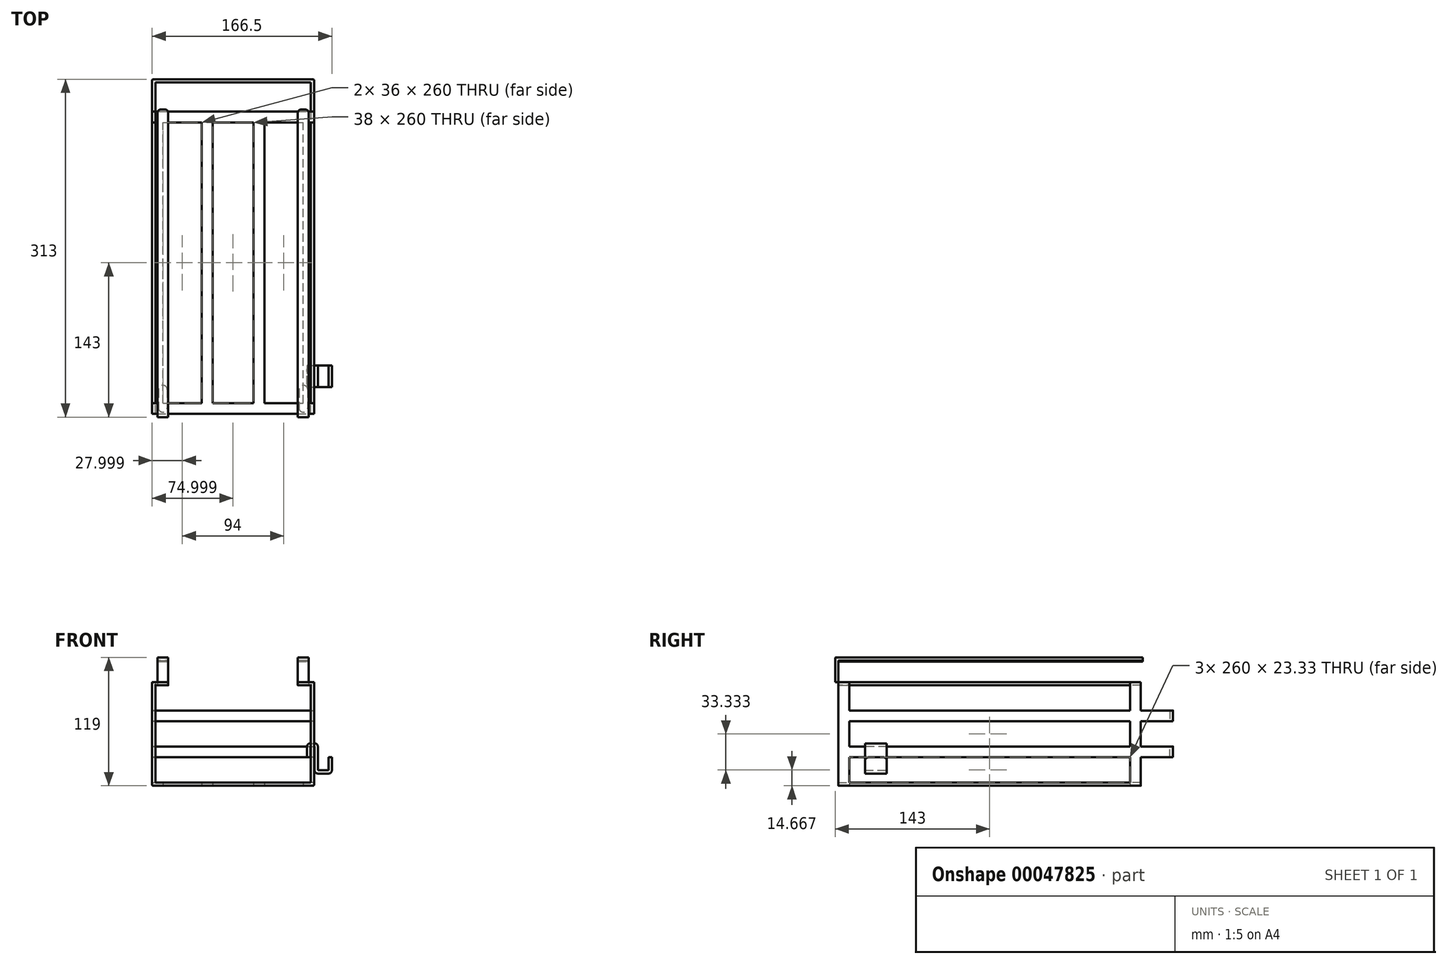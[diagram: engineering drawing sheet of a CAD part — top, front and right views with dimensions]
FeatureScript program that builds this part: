
annotation { "Feature Type Name" : "Feature", "Feature Type Description" : "" }
export const myFeature = defineFeature(function(context is Context, id is Id, definition is map)
    precondition{}
    {
        {
            var Q0;
            Q0=qCreatedBy(makeId("Top.planeOp"),FACE);
            var sketch = newSketch(context, id + "F0", { "sketchPlane" : qUnion([Q0])});
            skLineSegment(sketch, "E0.bottom", {"start": v(-155.28, 215.65) * mm, "end": v(-5.28, 215.65) * mm});
            skLineSegment(sketch, "E0.top", {"start": v(-155.28, -94.35) * mm, "end": v(-5.28, -94.35) * mm});
            skLineSegment(sketch, "E0.left", {"start": v(-155.28, 215.65) * mm, "end": v(-155.28, -94.35) * mm});
            skLineSegment(sketch, "E0.right", {"start": v(-5.28, 215.65) * mm, "end": v(-5.28, -94.35) * mm});
            skLineSegment(sketch, "E1", {"start": v(-155.28, -84.35) * mm, "end": v(-5.28, -84.35) * mm});
            skLineSegment(sketch, "E2", {"start": v(-109.28, -84.35) * mm, "end": v(-109.28, 175.65) * mm});
            skLineSegment(sketch, "E3.0", {"start": v(-99.28, -84.35) * mm, "end": v(-99.28, 175.65) * mm});
            skLineSegment(sketch, "E4", {"start": v(-61.28, -84.35) * mm, "end": v(-61.28, 175.65) * mm});
            skLineSegment(sketch, "E5.0", {"start": v(-51.28, -84.35) * mm, "end": v(-51.28, 175.65) * mm});
            skLineSegment(sketch, "E6", {"start": v(-45.28, -42.82) * mm, "end": v(-5.28, -42.82) * mm, "construction": true});
            skLineSegment(sketch, "E7", {"start": v(-155.28, 175.65) * mm, "end": v(-5.28, 175.65) * mm});
            skLineSegment(sketch, "E8.0", {"start": v(-155.28, 185.65) * mm, "end": v(-5.28, 185.65) * mm});
            skLineSegment(sketch, "E9", {"start": v(-145.28, -84.35) * mm, "end": v(-145.28, 175.65) * mm});
            skLineSegment(sketch, "E10", {"start": v(-15.28, -84.35) * mm, "end": v(-15.28, 175.65) * mm});
            skSolve(sketch);
        }
        {
            var Q0;
            {var subQ13=sQuery(id+"F0.wireOp",EDGE,"E8.0");Q0=makeQuery(id+"F0.imprint","IMPRINT",FACE,{"disambiguationData":[TD([[makeQuery(id+"F0.imprint","IMPRINT",EDGE,{"derivedFrom":subQ13}),-1.0]])]});}
            var Q1;
            {var subQ2=sQuery(id+"F0.wireOp",EDGE,"E2");Q1=makeQuery(id+"F0.imprint","IMPRINT",FACE,{"disambiguationData":[TD([[makeQuery(id+"F0.imprint","IMPRINT",EDGE,{"derivedFrom":subQ2}),-1.0]])]});}
            var Q2;
            {var subQ2=sQuery(id+"F0.wireOp",EDGE,"E4");Q2=makeQuery(id+"F0.imprint","IMPRINT",FACE,{"disambiguationData":[TD([[makeQuery(id+"F0.imprint","IMPRINT",EDGE,{"derivedFrom":subQ2}),-1.0]])]});}
            var Q3;
            {var subQ2=sQuery(id+"F0.wireOp",EDGE,"25806873-daf4-42d4-93ea-269611503551.0");Q3=makeQuery(id+"F0.imprint","IMPRINT",FACE,{"disambiguationData":[TD([[makeQuery(id+"F0.imprint","IMPRINT",EDGE,{"derivedFrom":subQ2}),-1.0]])]});}
            var Q4;
            {var subQ2=sQuery(id+"F0.wireOp",EDGE,"f27c75fe-956d-4c7f-83a3-ad04fe21480e.0");Q4=makeQuery(id+"F0.imprint","IMPRINT",FACE,{"disambiguationData":[TD([[makeQuery(id+"F0.imprint","IMPRINT",EDGE,{"derivedFrom":subQ2}),-1.0]])]});}
            var Q5;
            {var subQ2=sQuery(id+"F0.wireOp",EDGE,"57173786-8ee7-4b31-aee3-b8c71c6fc913.0");Q5=makeQuery(id+"F0.imprint","IMPRINT",FACE,{"disambiguationData":[TD([[makeQuery(id+"F0.imprint","IMPRINT",EDGE,{"derivedFrom":subQ2}),-1.0]])]});}
            var Q6;
            {var subQ2=sQuery(id+"F0.wireOp",EDGE,"b295c677-741d-4f0f-b40e-4d89e7042368.0");Q6=makeQuery(id+"F0.imprint","IMPRINT",FACE,{"disambiguationData":[TD([[makeQuery(id+"F0.imprint","IMPRINT",EDGE,{"derivedFrom":subQ2}),-1.0]])]});}
            var Q7;
            {var subQ6=sQuery(id+"F0.wireOp",EDGE,"E0.top");Q7=makeQuery(id+"F0.imprint","IMPRINT",FACE,{"disambiguationData":[TD([[makeQuery(id+"F0.imprint","IMPRINT",EDGE,{"derivedFrom":subQ6}),1.0]])]});}
            var Q8;
            {var subQ0=sQuery(id+"F0.wireOp",EDGE,"E9");Q8=makeQuery(id+"F0.imprint","IMPRINT",FACE,{"disambiguationData":[TD([[makeQuery(id+"F0.imprint","IMPRINT",EDGE,{"derivedFrom":subQ0}),1.0]])]});}
            var Q9;
            {var subQ0=sQuery(id+"F0.wireOp",EDGE,"E10");Q9=makeQuery(id+"F0.imprint","IMPRINT",FACE,{"disambiguationData":[TD([[makeQuery(id+"F0.imprint","IMPRINT",EDGE,{"derivedFrom":subQ0}),-1.0]])]});}
            extrude(context, id + "F1", {"entities" : qUnion([Q0, Q1, Q2, Q3, Q4, Q5, Q6, Q7, Q8, Q9]), "depth" : 3 * mm});
        }
        {
            var Q0;
            Q0=makeQuery(id+"F1.opExtrude","CAP_FACE",FACE,{"disambiguationData":[OSD([sQuery(id+"F0.wireOp",EDGE,"E0.top"),sQuery(id+"F0.wireOp",EDGE,"E0.left"),sQuery(id+"F0.wireOp",EDGE,"E0.right"),sQuery(id+"F0.wireOp",EDGE,"E1"),sQuery(id+"F0.wireOp",EDGE,"E2"),sQuery(id+"F0.wireOp",EDGE,"E3.0"),sQuery(id+"F0.wireOp",EDGE,"E4"),sQuery(id+"F0.wireOp",EDGE,"E5.0"),sQuery(id+"F0.wireOp",EDGE,"25806873-daf4-42d4-93ea-269611503551.0"),sQuery(id+"F0.wireOp",EDGE,"183b0f32-b38d-4a6b-b23a-afe10f441196.0"),sQuery(id+"F0.wireOp",EDGE,"f27c75fe-956d-4c7f-83a3-ad04fe21480e.0"),sQuery(id+"F0.wireOp",EDGE,"ded52414-d426-43c9-a379-c6c363a8f75c.0"),sQuery(id+"F0.wireOp",EDGE,"57173786-8ee7-4b31-aee3-b8c71c6fc913.0"),sQuery(id+"F0.wireOp",EDGE,"5944464c-8a10-4b62-a13b-28cb052c5347.0"),sQuery(id+"F0.wireOp",EDGE,"b295c677-741d-4f0f-b40e-4d89e7042368.0"),sQuery(id+"F0.wireOp",EDGE,"6ecef191-8e82-4d4f-89e7-14b12a768c5f.0"),sQuery(id+"F0.wireOp",EDGE,"E7"),sQuery(id+"F0.wireOp",EDGE,"E8.0")])],"isStart":false});
            var sketch = newSketch(context, id + "F2", { "sketchPlane" : qUnion([Q0])});
            skLineSegment(sketch, "E11.bottom", {"start": v(-155.28, 185.65) * mm, "end": v(-152.28, 185.65) * mm});
            skLineSegment(sketch, "E11.top", {"start": v(-155.28, 175.65) * mm, "end": v(-152.28, 175.65) * mm});
            skLineSegment(sketch, "E11.left", {"start": v(-155.28, 185.65) * mm, "end": v(-155.28, 175.65) * mm});
            skLineSegment(sketch, "E11.right", {"start": v(-152.28, 185.65) * mm, "end": v(-152.28, 175.65) * mm});
            skLineSegment(sketch, "E12.bottom", {"start": v(-155.28, -94.35) * mm, "end": v(-152.28, -94.35) * mm});
            skLineSegment(sketch, "E12.top", {"start": v(-155.28, -84.35) * mm, "end": v(-152.28, -84.35) * mm});
            skLineSegment(sketch, "E12.left", {"start": v(-155.28, -94.35) * mm, "end": v(-155.28, -84.35) * mm});
            skLineSegment(sketch, "E12.right", {"start": v(-152.28, -94.35) * mm, "end": v(-152.28, -84.35) * mm});
            skLineSegment(sketch, "E13", {"start": v(-80.28, 152.07) * mm, "end": v(-80.28, 185.65) * mm, "construction": true});
            skLineSegment(sketch, "E14.MirrorCS", {"start": v(-8.28, 185.65) * mm, "end": v(-8.28, 175.65) * mm});
            skLineSegment(sketch, "E15.MirrorCS", {"start": v(-5.28, 185.65) * mm, "end": v(-5.28, 175.65) * mm});
            skLineSegment(sketch, "E16.MirrorCS", {"start": v(-5.28, 185.65) * mm, "end": v(-8.28, 185.65) * mm});
            skLineSegment(sketch, "E17.MirrorCS", {"start": v(-5.28, 175.65) * mm, "end": v(-8.28, 175.65) * mm});
            skLineSegment(sketch, "E18.MirrorCS", {"start": v(-8.28, -94.35) * mm, "end": v(-8.28, -84.35) * mm});
            skLineSegment(sketch, "E19.MirrorCS", {"start": v(-5.28, -94.35) * mm, "end": v(-5.28, -84.35) * mm});
            skLineSegment(sketch, "E20.MirrorCS", {"start": v(-5.28, -84.35) * mm, "end": v(-8.28, -84.35) * mm});
            skLineSegment(sketch, "E21.MirrorCS", {"start": v(-5.28, -94.35) * mm, "end": v(-8.28, -94.35) * mm});
            skSolve(sketch);
        }
        {
            var Q0;
            Q0=makeQuery(id+"F2.imprint","IMPRINT",FACE,{"disambiguationData":[TD([[makeQuery(id+"F2.imprint","IMPRINT",EDGE,{"derivedFrom":sQuery(id+"F2.wireOp",EDGE,"E11.bottom")}),-1.0]])]});
            var Q1;
            Q1=makeQuery(id+"F2.imprint","IMPRINT",FACE,{"disambiguationData":[TD([[makeQuery(id+"F2.imprint","IMPRINT",EDGE,{"derivedFrom":sQuery(id+"F2.wireOp",EDGE,"E14.MirrorCS")}),1.0]])]});
            var Q2;
            Q2=makeQuery(id+"F2.imprint","IMPRINT",FACE,{"disambiguationData":[TD([[makeQuery(id+"F2.imprint","IMPRINT",EDGE,{"derivedFrom":sQuery(id+"F2.wireOp",EDGE,"E18.MirrorCS")}),-1.0]])]});
            var Q3;
            Q3=makeQuery(id+"F2.imprint","IMPRINT",FACE,{"disambiguationData":[TD([[makeQuery(id+"F2.imprint","IMPRINT",EDGE,{"derivedFrom":sQuery(id+"F2.wireOp",EDGE,"E12.bottom")}),1.0]])]});
            extrude(context, id + "F3", {"entities" : qUnion([Q0, Q1, Q2, Q3]), "operationType" : NewBodyOperationType.ADD, "depth" : 90 * mm});
        }
        {
            var Q0;
            Q0=makeQuery(id+"F3.opExtrude","CAP_FACE",FACE,{"disambiguationData":[OSD([sQuery(id+"F2.wireOp",EDGE,"E11.bottom"),sQuery(id+"F2.wireOp",EDGE,"E11.top"),sQuery(id+"F2.wireOp",EDGE,"E11.left"),sQuery(id+"F2.wireOp",EDGE,"E11.right")])],"isStart":false});
            var sketch = newSketch(context, id + "F4", { "sketchPlane" : qUnion([Q0])});
            skLineSegment(sketch, "E22.bottom", {"start": v(-150.28, 185.65) * mm, "end": v(-140.28, 185.65) * mm});
            skLineSegment(sketch, "E22.top", {"start": v(-150.28, -94.35) * mm, "end": v(-140.28, -94.35) * mm});
            skLineSegment(sketch, "E22.left", {"start": v(-150.28, 185.65) * mm, "end": v(-150.28, -94.35) * mm});
            skLineSegment(sketch, "E22.right", {"start": v(-140.28, 185.65) * mm, "end": v(-140.28, -94.35) * mm});
            skLineSegment(sketch, "E23.MirrorCS", {"start": v(-20.28, 185.65) * mm, "end": v(-20.28, -94.35) * mm});
            skLineSegment(sketch, "E24.MirrorCS", {"start": v(-10.28, 185.65) * mm, "end": v(-10.28, -94.35) * mm});
            skLineSegment(sketch, "E25.MirrorCS", {"start": v(-10.28, 185.65) * mm, "end": v(-20.28, 185.65) * mm});
            skLineSegment(sketch, "E26.MirrorCS", {"start": v(-10.28, -94.35) * mm, "end": v(-20.28, -94.35) * mm});
            skLineSegment(sketch, "E27.bottom", {"start": v(-150.28, -94.35) * mm, "end": v(-155.28, -94.35) * mm});
            skLineSegment(sketch, "E27.top", {"start": v(-150.28, -84.35) * mm, "end": v(-155.28, -84.35) * mm});
            skLineSegment(sketch, "E27.left", {"start": v(-150.28, -94.35) * mm, "end": v(-150.28, -84.35) * mm});
            skLineSegment(sketch, "E27.right", {"start": v(-155.28, -94.35) * mm, "end": v(-155.28, -84.35) * mm});
            skLineSegment(sketch, "E28.MirrorCS", {"start": v(-10.28, -84.35) * mm, "end": v(-5.28, -84.35) * mm});
            skLineSegment(sketch, "E29.MirrorCS", {"start": v(-5.28, -94.35) * mm, "end": v(-5.28, -84.35) * mm});
            skLineSegment(sketch, "E30.MirrorCS", {"start": v(-10.28, -94.35) * mm, "end": v(-5.28, -94.35) * mm});
            skLineSegment(sketch, "E31.bottom", {"start": v(-150.28, 185.65) * mm, "end": v(-155.28, 185.65) * mm});
            skLineSegment(sketch, "E31.top", {"start": v(-150.28, 175.65) * mm, "end": v(-155.28, 175.65) * mm});
            skLineSegment(sketch, "E31.left", {"start": v(-150.28, 185.65) * mm, "end": v(-150.28, 175.65) * mm});
            skLineSegment(sketch, "E31.right", {"start": v(-155.28, 185.65) * mm, "end": v(-155.28, 175.65) * mm});
            skLineSegment(sketch, "E32.MirrorCS", {"start": v(-10.28, 175.65) * mm, "end": v(-5.28, 175.65) * mm});
            skLineSegment(sketch, "E33.MirrorCS", {"start": v(-10.28, 185.65) * mm, "end": v(-5.28, 185.65) * mm});
            skLineSegment(sketch, "E34.MirrorCS", {"start": v(-5.28, 185.65) * mm, "end": v(-5.28, 175.65) * mm});
            skLineSegment(sketch, "E35.bottom", {"start": v(-140.28, -94.35) * mm, "end": v(-150.28, -94.35) * mm});
            skLineSegment(sketch, "E35.top", {"start": v(-140.28, -97.35) * mm, "end": v(-150.28, -97.35) * mm});
            skLineSegment(sketch, "E35.left", {"start": v(-140.28, -94.35) * mm, "end": v(-140.28, -97.35) * mm});
            skLineSegment(sketch, "E35.right", {"start": v(-150.28, -94.35) * mm, "end": v(-150.28, -97.35) * mm});
            skLineSegment(sketch, "E36.top", {"start": v(-10.28, -97.35) * mm, "end": v(-20.28, -97.35) * mm});
            skLineSegment(sketch, "E36.left", {"start": v(-10.28, -94.35) * mm, "end": v(-10.28, -97.35) * mm});
            skLineSegment(sketch, "E36.right", {"start": v(-20.28, -94.35) * mm, "end": v(-20.28, -97.35) * mm});
            skSolve(sketch);
        }
        {
            var Q0;
            Q0=makeQuery(id+"F4.imprint","IMPRINT",FACE,{"disambiguationData":[TD([[makeQuery(id+"F4.imprint","IMPRINT",EDGE,{"derivedFrom":sQuery(id+"F4.wireOp",EDGE,"E22.bottom")}),-1.0]])]});
            var Q1;
            {var subQ1=sQuery(id+"F4.wireOp",EDGE,"E31.left");Q1=makeQuery(id+"F4.imprint","IMPRINT",FACE,{"disambiguationData":[TD([[makeQuery(id+"F4.imprint","IMPRINT",EDGE,{"derivedFrom":subQ1}),-1.0]])]});}
            var Q2;
            {var subQ1=sQuery(id+"F4.wireOp",EDGE,"E31.right");Q2=makeQuery(id+"F4.imprint","IMPRINT",FACE,{"disambiguationData":[TD([[makeQuery(id+"F4.imprint","IMPRINT",EDGE,{"derivedFrom":subQ1}),1.0]])]});}
            var Q3;
            Q3=makeQuery(id+"F4.imprint","IMPRINT",FACE,{"disambiguationData":[TD([[makeQuery(id+"F4.imprint","IMPRINT",EDGE,{"derivedFrom":sQuery(id+"F4.wireOp",EDGE,"E35.bottom")}),1.0]])]});
            var Q4;
            Q4=makeQuery(id+"F4.imprint","IMPRINT",FACE,{"disambiguationData":[TD([[makeQuery(id+"F4.imprint","IMPRINT",EDGE,{"derivedFrom":sQuery(id+"F4.wireOp",EDGE,"E26.MirrorCS")}),1.0]])]});
            var Q5;
            Q5=makeQuery(id+"F4.imprint","IMPRINT",FACE,{"disambiguationData":[TD([[makeQuery(id+"F4.imprint","IMPRINT",EDGE,{"derivedFrom":sQuery(id+"F4.wireOp",EDGE,"E23.MirrorCS")}),1.0]])]});
            var Q6;
            {var subQ1=sQuery(id+"F4.wireOp",EDGE,"E28.MirrorCS");Q6=makeQuery(id+"F4.imprint","IMPRINT",FACE,{"disambiguationData":[TD([[makeQuery(id+"F4.imprint","IMPRINT",EDGE,{"derivedFrom":subQ1}),-1.0]])]});}
            var Q7;
            {var subQ1=sQuery(id+"F4.wireOp",EDGE,"E32.MirrorCS");Q7=makeQuery(id+"F4.imprint","IMPRINT",FACE,{"disambiguationData":[TD([[makeQuery(id+"F4.imprint","IMPRINT",EDGE,{"derivedFrom":subQ1}),1.0]])]});}
            var Q8;
            Q8=makeQuery(id+"F4.imprint","IMPRINT",FACE,{"disambiguationData":[TD([[makeQuery(id+"F4.imprint","IMPRINT",EDGE,{"derivedFrom":sQuery(id+"F4.wireOp",EDGE,"E27.bottom")}),-1.0]])]});
            extrude(context, id + "F5", {"entities" : qUnion([Q0, Q1, Q2, Q3, Q4, Q5, Q6, Q7, Q8]), "operationType" : NewBodyOperationType.ADD, "depth" : 3 * mm});
        }
        {
            var Q0;
            Q0=makeQuery(id+"F5.opExtrude","CAP_FACE",FACE,{"disambiguationData":[OSD([sQuery(id+"F4.wireOp",EDGE,"E22.bottom"),sQuery(id+"F4.wireOp",EDGE,"E22.top"),sQuery(id+"F4.wireOp",EDGE,"E22.left"),sQuery(id+"F4.wireOp",EDGE,"E22.right")])],"isStart":false});
            var sketch = newSketch(context, id + "F6", { "sketchPlane" : qUnion([Q0])});
            skLineSegment(sketch, "E37.bottom", {"start": v(-140.28, -97.35) * mm, "end": v(-150.28, -97.35) * mm});
            skLineSegment(sketch, "E37.top", {"start": v(-140.28, -94.35) * mm, "end": v(-150.28, -94.35) * mm});
            skLineSegment(sketch, "E37.left", {"start": v(-140.28, -97.35) * mm, "end": v(-140.28, -94.35) * mm});
            skLineSegment(sketch, "E37.right", {"start": v(-150.28, -97.35) * mm, "end": v(-150.28, -94.35) * mm});
            skLineSegment(sketch, "E38.MirrorCS", {"start": v(-20.28, -94.35) * mm, "end": v(-10.28, -94.35) * mm});
            skLineSegment(sketch, "E39.MirrorCS", {"start": v(-10.28, -97.35) * mm, "end": v(-10.28, -94.35) * mm});
            skLineSegment(sketch, "E40.MirrorCS", {"start": v(-20.28, -97.35) * mm, "end": v(-20.28, -94.35) * mm});
            skLineSegment(sketch, "E41.MirrorCS", {"start": v(-20.28, -97.35) * mm, "end": v(-10.28, -97.35) * mm});
            skSolve(sketch);
        }
        {
            var Q0;
            Q0=makeQuery(id+"F6.imprint","IMPRINT",FACE,{"disambiguationData":[TD([[makeQuery(id+"F6.imprint","IMPRINT",EDGE,{"derivedFrom":sQuery(id+"F6.wireOp",EDGE,"E37.bottom")}),-1.0]])]});
            var Q1;
            Q1=makeQuery(id+"F6.imprint","IMPRINT",FACE,{"disambiguationData":[TD([[makeQuery(id+"F6.imprint","IMPRINT",EDGE,{"derivedFrom":sQuery(id+"F6.wireOp",EDGE,"E38.MirrorCS")}),-1.0]])]});
            extrude(context, id + "F7", {"entities" : qUnion([Q0, Q1]), "operationType" : NewBodyOperationType.ADD, "depth" : 20 * mm});
        }
        {
            var Q0;
            Q0=makeQuery(id+"F7.opExtrude","CAP_FACE",FACE,{"disambiguationData":[OSD([sQuery(id+"F6.wireOp",EDGE,"E37.bottom"),sQuery(id+"F6.wireOp",EDGE,"E37.top"),sQuery(id+"F6.wireOp",EDGE,"E37.left"),sQuery(id+"F6.wireOp",EDGE,"E37.right")])],"isStart":false});
            var sketch = newSketch(context, id + "F8", { "sketchPlane" : qUnion([Q0])});
            skLineSegment(sketch, "E42.bottom", {"start": v(-150.28, -97.35) * mm, "end": v(-140.28, -97.35) * mm});
            skLineSegment(sketch, "E42.top", {"start": v(-150.28, 187.65) * mm, "end": v(-140.28, 187.65) * mm});
            skLineSegment(sketch, "E42.left", {"start": v(-150.28, -97.35) * mm, "end": v(-150.28, 187.65) * mm});
            skLineSegment(sketch, "E42.right", {"start": v(-140.28, -97.35) * mm, "end": v(-140.28, 187.65) * mm});
            skLineSegment(sketch, "E43.MirrorCS", {"start": v(-20.28, -97.35) * mm, "end": v(-20.28, 187.65) * mm});
            skLineSegment(sketch, "E44.MirrorCS", {"start": v(-10.28, 187.65) * mm, "end": v(-20.28, 187.65) * mm});
            skLineSegment(sketch, "E45.MirrorCS", {"start": v(-10.28, -97.35) * mm, "end": v(-10.28, 187.65) * mm});
            skLineSegment(sketch, "E46.MirrorCS", {"start": v(-10.28, -97.35) * mm, "end": v(-20.28, -97.35) * mm});
            skPoint(sketch, "E47", {"position": v(-140.28, 45.15) * mm});
            skSolve(sketch);
        }
        {
            var Q0;
            {var subQ1=sQuery(id+"F8.wireOp",EDGE,"E42.top");Q0=makeQuery(id+"F8.imprint","IMPRINT",FACE,{"disambiguationData":[TD([[makeQuery(id+"F8.imprint","IMPRINT",EDGE,{"derivedFrom":subQ1}),-1.0]])]});}
            var Q1;
            Q1=makeQuery(id+"F8.imprint","IMPRINT",FACE,{"disambiguationData":[TD([[makeQuery(id+"F8.imprint","IMPRINT",EDGE,{"derivedFrom":sQuery(id+"F8.wireOp",EDGE,"E43.MirrorCS")}),-1.0]])]});
            var Q2;
            {var subQ2=sQuery(id+"F8.wireOp",EDGE,"E42.bottom");Q2=makeQuery(id+"F8.imprint","IMPRINT",FACE,{"disambiguationData":[TD([[makeQuery(id+"F8.imprint","IMPRINT",EDGE,{"derivedFrom":subQ2}),1.0]])]});}
            var Q3;
            {var subQ2=sQuery(id+"F8.wireOp",EDGE,"E42.bottom");Q3=makeQuery(id+"F8.imprint","IMPRINT",FACE,{"disambiguationData":[TD([[makeQuery(id+"F8.imprint","IMPRINT",EDGE,{"derivedFrom":subQ2}),-1.0]])]});}
            extrude(context, id + "F9", {"entities" : qUnion([Q0, Q1, Q2, Q3]), "operationType" : NewBodyOperationType.ADD, "depth" : 3 * mm});
        }
        {
            var Q0;
            Q0=makeQuery(id+"F5.boolean.opBoolean","MERGE",FACE,{"derivedFrom":[makeQuery(id+"F3.boolean.opBoolean","MERGE",FACE,{"derivedFrom":[makeQuery(id+"F1.opExtrude","SWEPT_FACE",FACE,{"disambiguationData":[OSD([sQuery(id+"F0.wireOp",EDGE,"E8.0")])]}),makeQuery(id+"F3.opExtrude","SWEPT_FACE",FACE,{"disambiguationData":[OSD([sQuery(id+"F2.wireOp",EDGE,"E11.bottom")])]}),makeQuery(id+"F3.opExtrude","SWEPT_FACE",FACE,{"disambiguationData":[OSD([sQuery(id+"F2.wireOp",EDGE,"E16.MirrorCS")])]})]}),makeQuery(id+"F5.opExtrude","SWEPT_FACE",FACE,{"disambiguationData":[OSD([sQuery(id+"F4.wireOp",EDGE,"E22.bottom")])]}),makeQuery(id+"F5.opExtrude","SWEPT_FACE",FACE,{"disambiguationData":[OSD([sQuery(id+"F4.wireOp",EDGE,"E25.MirrorCS")])]})]});
            var sketch = newSketch(context, id + "F10", { "sketchPlane" : qUnion([Q0])});
            skLineSegment(sketch, "E48", {"start": v(152.28, 3) * mm, "end": v(155.28, 3) * mm, "construction": true});
            skLineSegment(sketch, "E49", {"start": v(152.28, 93) * mm, "end": v(155.28, 93) * mm, "construction": true});
            skLineSegment(sketch, "E50.bottom", {"start": v(155.28, 69.67) * mm, "end": v(152.28, 69.67) * mm});
            skLineSegment(sketch, "E50.top", {"start": v(155.28, 59.67) * mm, "end": v(152.28, 59.67) * mm});
            skLineSegment(sketch, "E50.left", {"start": v(155.28, 69.67) * mm, "end": v(155.28, 59.67) * mm});
            skLineSegment(sketch, "E50.right", {"start": v(152.28, 69.67) * mm, "end": v(152.28, 59.67) * mm});
            skLineSegment(sketch, "E51.bottom", {"start": v(155.28, 36.33) * mm, "end": v(152.28, 36.33) * mm});
            skLineSegment(sketch, "E51.top", {"start": v(155.28, 26.33) * mm, "end": v(152.28, 26.33) * mm});
            skLineSegment(sketch, "E51.left", {"start": v(155.28, 36.33) * mm, "end": v(155.28, 26.33) * mm});
            skLineSegment(sketch, "E51.right", {"start": v(152.28, 36.33) * mm, "end": v(152.28, 26.33) * mm});
            skLineSegment(sketch, "E52", {"start": v(153.78, 93) * mm, "end": v(153.78, 69.67) * mm, "construction": true});
            skLineSegment(sketch, "E53", {"start": v(153.78, 59.67) * mm, "end": v(153.78, 36.33) * mm, "construction": true});
            skLineSegment(sketch, "E54", {"start": v(153.78, 26.33) * mm, "end": v(153.78, 3) * mm, "construction": true});
            skLineSegment(sketch, "E55", {"start": v(80.28, 3) * mm, "end": v(80.28, 25.42) * mm, "construction": true});
            skLineSegment(sketch, "E56.MirrorCS", {"start": v(5.28, 26.33) * mm, "end": v(8.28, 26.33) * mm});
            skLineSegment(sketch, "E57.MirrorCS", {"start": v(5.28, 36.33) * mm, "end": v(8.28, 36.33) * mm});
            skLineSegment(sketch, "E58.MirrorCS", {"start": v(8.28, 36.33) * mm, "end": v(8.28, 26.33) * mm});
            skLineSegment(sketch, "E59.MirrorCS", {"start": v(5.28, 36.33) * mm, "end": v(5.28, 26.33) * mm});
            skLineSegment(sketch, "E60.MirrorCS", {"start": v(5.28, 59.67) * mm, "end": v(8.28, 59.67) * mm});
            skLineSegment(sketch, "E61.MirrorCS", {"start": v(8.28, 69.67) * mm, "end": v(8.28, 59.67) * mm});
            skLineSegment(sketch, "E62.MirrorCS", {"start": v(5.28, 69.67) * mm, "end": v(5.28, 59.67) * mm});
            skLineSegment(sketch, "E63.MirrorCS", {"start": v(5.28, 69.67) * mm, "end": v(8.28, 69.67) * mm});
            skSolve(sketch);
        }
        {
            var Q0;
            Q0=makeQuery(id+"F10.imprint","IMPRINT",FACE,{"disambiguationData":[TD([[makeQuery(id+"F10.imprint","IMPRINT",EDGE,{"derivedFrom":sQuery(id+"F10.wireOp",EDGE,"E50.bottom")}),1.0]])]});
            var Q1;
            Q1=makeQuery(id+"F10.imprint","IMPRINT",FACE,{"disambiguationData":[TD([[makeQuery(id+"F10.imprint","IMPRINT",EDGE,{"derivedFrom":sQuery(id+"F10.wireOp",EDGE,"E51.bottom")}),1.0]])]});
            var Q2;
            Q2=makeQuery(id+"F10.imprint","IMPRINT",FACE,{"disambiguationData":[TD([[makeQuery(id+"F10.imprint","IMPRINT",EDGE,{"derivedFrom":sQuery(id+"F10.wireOp",EDGE,"E60.MirrorCS")}),1.0]])]});
            var Q3;
            Q3=makeQuery(id+"F10.imprint","IMPRINT",FACE,{"disambiguationData":[TD([[makeQuery(id+"F10.imprint","IMPRINT",EDGE,{"derivedFrom":sQuery(id+"F10.wireOp",EDGE,"E56.MirrorCS")}),1.0]])]});
            var Q4;
            Q4=makeQuery(id+"F5.boolean.opBoolean","MERGE",FACE,{"derivedFrom":[makeQuery(id+"F3.opExtrude","SWEPT_FACE",FACE,{"disambiguationData":[OSD([sQuery(id+"F2.wireOp",EDGE,"E12.top")])]}),makeQuery(id+"F5.opExtrude","SWEPT_FACE",FACE,{"disambiguationData":[OSD([sQuery(id+"F4.wireOp",EDGE,"E27.top")])]})]});
            extrude(context, id + "F11", {"entities" : qUnion([Q0, Q1, Q2, Q3]), "operationType" : NewBodyOperationType.ADD, "depth" : 30 * mm, "hasSecondDirection" : true, "secondDirectionBound" : SecondDirectionBoundingType.UP_TO_SURFACE, "secondDirectionOppositeDirection" : true, "secondDirectionBoundEntityFace" : qUnion([Q4]), "secondDirectionDepth" : 25 * mm});
        }
        {
            var Q0;
            Q0=makeQuery(id+"F11.boolean.opBoolean","MERGE",FACE,{"derivedFrom":[makeQuery(id+"F3.opExtrude","SWEPT_FACE",FACE,{"disambiguationData":[OSD([sQuery(id+"F2.wireOp",EDGE,"E11.right")])]}),makeQuery(id+"F3.opExtrude","SWEPT_FACE",FACE,{"disambiguationData":[OSD([sQuery(id+"F2.wireOp",EDGE,"E12.right")])]}),makeQuery(id+"F11.opExtrude","SWEPT_FACE",FACE,{"disambiguationData":[OSD([sQuery(id+"F10.wireOp",EDGE,"E50.right")])]}),makeQuery(id+"F11.opExtrude","SWEPT_FACE",FACE,{"disambiguationData":[OSD([sQuery(id+"F10.wireOp",EDGE,"E51.right")])]})]});
            var sketch = newSketch(context, id + "F12", { "sketchPlane" : qUnion([Q0])});
            skLineSegment(sketch, "E64.bottom", {"start": v(215.65, 69.67) * mm, "end": v(212.65, 69.67) * mm});
            skLineSegment(sketch, "E64.top", {"start": v(215.65, 59.67) * mm, "end": v(212.65, 59.67) * mm});
            skLineSegment(sketch, "E64.left", {"start": v(215.65, 69.67) * mm, "end": v(215.65, 59.67) * mm});
            skLineSegment(sketch, "E64.right", {"start": v(212.65, 69.67) * mm, "end": v(212.65, 59.67) * mm});
            skLineSegment(sketch, "E65.bottom", {"start": v(215.65, 26.33) * mm, "end": v(212.65, 26.33) * mm});
            skLineSegment(sketch, "E65.top", {"start": v(215.65, 36.33) * mm, "end": v(212.65, 36.33) * mm});
            skLineSegment(sketch, "E65.left", {"start": v(215.65, 26.33) * mm, "end": v(215.65, 36.33) * mm});
            skLineSegment(sketch, "E65.right", {"start": v(212.65, 26.33) * mm, "end": v(212.65, 36.33) * mm});
            skSolve(sketch);
        }
        {
            var Q0;
            Q0=makeQuery(id+"F12.imprint","IMPRINT",FACE,{"disambiguationData":[TD([[makeQuery(id+"F12.imprint","IMPRINT",EDGE,{"derivedFrom":sQuery(id+"F12.wireOp",EDGE,"E64.bottom")}),1.0]])]});
            var Q1;
            Q1=makeQuery(id+"F12.imprint","IMPRINT",FACE,{"disambiguationData":[TD([[makeQuery(id+"F12.imprint","IMPRINT",EDGE,{"derivedFrom":sQuery(id+"F12.wireOp",EDGE,"E65.bottom")}),-1.0]])]});
            var Q2;
            Q2=makeQuery(id+"F11.boolean.opBoolean","MERGE",FACE,{"derivedFrom":[makeQuery(id+"F3.opExtrude","SWEPT_FACE",FACE,{"disambiguationData":[OSD([sQuery(id+"F2.wireOp",EDGE,"E14.MirrorCS")])]}),makeQuery(id+"F3.opExtrude","SWEPT_FACE",FACE,{"disambiguationData":[OSD([sQuery(id+"F2.wireOp",EDGE,"E18.MirrorCS")])]}),makeQuery(id+"F11.opExtrude","SWEPT_FACE",FACE,{"disambiguationData":[OSD([sQuery(id+"F10.wireOp",EDGE,"E58.MirrorCS")])]}),makeQuery(id+"F11.opExtrude","SWEPT_FACE",FACE,{"disambiguationData":[OSD([sQuery(id+"F10.wireOp",EDGE,"E61.MirrorCS")])]})]});
            extrude(context, id + "F13", {"entities" : qUnion([Q0, Q1]), "operationType" : NewBodyOperationType.ADD, "endBound" : BoundingType.UP_TO_SURFACE, "endBoundEntityFace" : qUnion([Q2]), "depth" : 25 * mm});
        }
        {
            var Q0;
            {var subQ0=sQuery(id+"F0.wireOp",EDGE,"E0.left");Q0=makeQuery(id+"F1.opExtrude","CAP_EDGE",EDGE,{"disambiguationData":[OSD([subQ0]),TDD([makeQuery(id+"F0.imprint","IMPRINT",EDGE,{"disambiguationData":[TD([[makeQuery(id+"F0.imprint","INTERSECT",VERTEX,{"derivedFrom":[subQ0,sQuery(id+"F0.wireOp",EDGE,"E7")]}),1.0]])],"derivedFrom":subQ0})])],"isStart":true});}
            var Q1;
            {var subQ0=sQuery(id+"F0.wireOp",EDGE,"E0.left");Q1=makeQuery(id+"F1.opExtrude","CAP_EDGE",EDGE,{"disambiguationData":[OSD([subQ0]),TDD([makeQuery(id+"F0.imprint","IMPRINT",EDGE,{"disambiguationData":[TD([[makeQuery(id+"F0.imprint","INTERSECT",VERTEX,{"derivedFrom":[sQuery(id+"F0.wireOp",EDGE,"E0.top"),subQ0]}),1.0]])],"derivedFrom":subQ0})])],"isStart":true});}
            var Q2;
            {var subQ0=sQuery(id+"F0.wireOp",EDGE,"E0.right");Q2=makeQuery(id+"F1.opExtrude","CAP_EDGE",EDGE,{"disambiguationData":[OSD([subQ0]),TDD([makeQuery(id+"F0.imprint","IMPRINT",EDGE,{"disambiguationData":[TD([[makeQuery(id+"F0.imprint","INTERSECT",VERTEX,{"derivedFrom":[sQuery(id+"F0.wireOp",EDGE,"E0.top"),subQ0]}),1.0]])],"derivedFrom":subQ0})])],"isStart":true});}
            var Q3;
            {var subQ0=sQuery(id+"F0.wireOp",EDGE,"E0.right");Q3=makeQuery(id+"F1.opExtrude","CAP_EDGE",EDGE,{"disambiguationData":[OSD([subQ0]),TDD([makeQuery(id+"F0.imprint","IMPRINT",EDGE,{"disambiguationData":[TD([[makeQuery(id+"F0.imprint","INTERSECT",VERTEX,{"derivedFrom":[subQ0,sQuery(id+"F0.wireOp",EDGE,"E7")]}),1.0]])],"derivedFrom":subQ0})])],"isStart":true});}
            var Q4;
            Q4=makeQuery(id+"F11.opExtrude","CAP_EDGE",EDGE,{"disambiguationData":[OSD([sQuery(id+"F10.wireOp",EDGE,"E59.MirrorCS")])],"isStart":false});
            var Q5;
            Q5=makeQuery(id+"F11.opExtrude","CAP_EDGE",EDGE,{"disambiguationData":[OSD([sQuery(id+"F10.wireOp",EDGE,"E62.MirrorCS")])],"isStart":false});
            var Q6;
            Q6=makeQuery(id+"F11.opExtrude","CAP_EDGE",EDGE,{"disambiguationData":[OSD([sQuery(id+"F10.wireOp",EDGE,"E50.left")])],"isStart":false});
            var Q7;
            Q7=makeQuery(id+"F11.opExtrude","CAP_EDGE",EDGE,{"disambiguationData":[OSD([sQuery(id+"F10.wireOp",EDGE,"E51.left")])],"isStart":false});
            var Q8;
            Q8=makeQuery(id+"F5.opExtrude","CAP_EDGE",EDGE,{"disambiguationData":[OSD([sQuery(id+"F4.wireOp",EDGE,"E22.left")])],"isStart":false});
            var Q9;
            Q9=makeQuery(id+"F9.opExtrude","CAP_EDGE",EDGE,{"disambiguationData":[OSD([sQuery(id+"F8.wireOp",EDGE,"E42.bottom")])],"isStart":false});
            var Q10;
            Q10=makeQuery(id+"F9.opExtrude","CAP_EDGE",EDGE,{"disambiguationData":[OSD([sQuery(id+"F8.wireOp",EDGE,"E46.MirrorCS")])],"isStart":false});
            var Q11;
            Q11=makeQuery(id+"F5.opExtrude","CAP_EDGE",EDGE,{"disambiguationData":[OSD([sQuery(id+"F4.wireOp",EDGE,"E24.MirrorCS")])],"isStart":false});
            var Q12;
            Q12=makeQuery(id+"F5.opExtrude","CAP_EDGE",EDGE,{"disambiguationData":[OSD([sQuery(id+"F4.wireOp",EDGE,"E22.top")])],"isStart":true});
            var Q13;
            Q13=makeQuery(id+"F5.opExtrude","CAP_EDGE",EDGE,{"disambiguationData":[OSD([sQuery(id+"F4.wireOp",EDGE,"E26.MirrorCS")])],"isStart":true});
            fillet(context, id + "F14", {"entities" : qUnion([Q0, Q1, Q2, Q3, Q4, Q5, Q6, Q7, Q8, Q9, Q10, Q11, Q12, Q13]), "radius" : 1 * mm, "tangentPropagation" : true, "allowEdgeOverflow" : false});
        }
        {
            var Q0;
            Q0=makeQuery(id+"F9.opExtrude","SWEPT_EDGE",EDGE,{"disambiguationData":[OSD([sQuery(id+"F8.wireOp",EDGE,"E42.top"),sQuery(id+"F8.wireOp",EDGE,"E42.right")])]});
            var Q1;
            Q1=makeQuery(id+"F9.opExtrude","SWEPT_EDGE",EDGE,{"disambiguationData":[OSD([sQuery(id+"F8.wireOp",EDGE,"E42.top"),sQuery(id+"F8.wireOp",EDGE,"E42.left")])]});
            var Q2;
            Q2=makeQuery(id+"F9.opExtrude","SWEPT_EDGE",EDGE,{"disambiguationData":[OSD([sQuery(id+"F8.wireOp",EDGE,"E43.MirrorCS"),sQuery(id+"F8.wireOp",EDGE,"E44.MirrorCS")])]});
            var Q3;
            Q3=makeQuery(id+"F9.opExtrude","SWEPT_EDGE",EDGE,{"disambiguationData":[OSD([sQuery(id+"F8.wireOp",EDGE,"E44.MirrorCS"),sQuery(id+"F8.wireOp",EDGE,"E45.MirrorCS")])]});
            fillet(context, id + "F15", {"entities" : qUnion([Q0, Q1, Q2, Q3]), "radius" : 3 * mm, "tangentPropagation" : true, "allowEdgeOverflow" : false});
        }
        {
            var Q0;
            Q0=makeQuery(id+"F9.opExtrude","CAP_FACE",FACE,{"disambiguationData":[OSD([sQuery(id+"F8.wireOp",EDGE,"E43.MirrorCS"),sQuery(id+"F8.wireOp",EDGE,"E44.MirrorCS"),sQuery(id+"F8.wireOp",EDGE,"E45.MirrorCS"),sQuery(id+"F8.wireOp",EDGE,"E46.MirrorCS")])],"isStart":true});
            var sketch = newSketch(context, id + "F16", { "sketchPlane" : qUnion([Q0])});
            skLineSegment(sketch, "E66.bottom", {"start": v(-19.22, -162.05) * mm, "end": v(-11.22, -162.05) * mm, "construction": true});
            skLineSegment(sketch, "E66.top", {"start": v(-19.22, -179.05) * mm, "end": v(-11.22, -179.05) * mm, "construction": true});
            skLineSegment(sketch, "E66.left", {"start": v(-19.22, -162.05) * mm, "end": v(-19.22, -179.05) * mm});
            skLineSegment(sketch, "E66.right", {"start": v(-11.22, -162.05) * mm, "end": v(-11.22, -179.05) * mm});
            skLineSegment(sketch, "E67", {"start": v(-140.28, -45.15) * mm, "end": v(-20.28, -45.15) * mm, "construction": true});
            skLineSegment(sketch, "E68", {"start": v(-80.28, -45.15) * mm, "end": v(-80.28, -56.72) * mm, "construction": true});
            skArc(sketch, "E69", {"start": v(-19.22, -179.05) * mm, "mid": v(-15.22, -183.05) * mm, "end": v(-11.22, -179.05) * mm});
            skArc(sketch, "E70", {"start": v(-11.22, -162.05) * mm, "mid": v(-15.22, -158.05) * mm, "end": v(-19.22, -162.05) * mm});
            skArc(sketch, "E71.MirrorCS", {"start": v(-19.22, 88.75) * mm, "mid": v(-15.22, 92.75) * mm, "end": v(-11.22, 88.75) * mm});
            skLineSegment(sketch, "E72.MirrorCS", {"start": v(-19.22, 71.75) * mm, "end": v(-19.22, 88.75) * mm});
            skLineSegment(sketch, "E73.MirrorCS", {"start": v(-11.22, 71.75) * mm, "end": v(-11.22, 88.75) * mm});
            skArc(sketch, "E74.MirrorCS", {"start": v(-11.22, 71.75) * mm, "mid": v(-15.22, 67.75) * mm, "end": v(-19.22, 71.75) * mm});
            skArc(sketch, "E75.MirrorCS", {"start": v(-141.35, -179.05) * mm, "mid": v(-145.35, -183.05) * mm, "end": v(-149.35, -179.05) * mm});
            skLineSegment(sketch, "E76.MirrorCS", {"start": v(-141.35, -162.05) * mm, "end": v(-141.35, -179.05) * mm});
            skLineSegment(sketch, "E77.MirrorCS", {"start": v(-149.35, -162.05) * mm, "end": v(-149.35, -179.05) * mm});
            skArc(sketch, "E78.MirrorCS", {"start": v(-149.35, -162.05) * mm, "mid": v(-145.35, -158.05) * mm, "end": v(-141.35, -162.05) * mm});
            skArc(sketch, "E79.MirrorCS", {"start": v(-149.35, 71.75) * mm, "mid": v(-145.35, 67.75) * mm, "end": v(-141.35, 71.75) * mm});
            skLineSegment(sketch, "E80.MirrorCS", {"start": v(-141.35, 71.75) * mm, "end": v(-141.35, 88.75) * mm});
            skArc(sketch, "E81.MirrorCS", {"start": v(-141.35, 88.75) * mm, "mid": v(-145.35, 92.75) * mm, "end": v(-149.35, 88.75) * mm});
            skLineSegment(sketch, "E82.MirrorCS", {"start": v(-149.35, 71.75) * mm, "end": v(-149.35, 88.75) * mm});
            skSolve(sketch);
        }
        {
            var Q0;
            Q0=makeQuery(id+"F16.imprint","IMPRINT",FACE,{"disambiguationData":[TD([[makeQuery(id+"F16.imprint","IMPRINT",EDGE,{"derivedFrom":sQuery(id+"F16.wireOp",EDGE,"E75.MirrorCS")}),-1.0]])]});
            var Q1;
            Q1=makeQuery(id+"F16.imprint","IMPRINT",FACE,{"disambiguationData":[TD([[makeQuery(id+"F16.imprint","IMPRINT",EDGE,{"derivedFrom":sQuery(id+"F16.wireOp",EDGE,"E66.left")}),1.0]])]});
            var Q2;
            Q2=makeQuery(id+"F16.imprint","IMPRINT",FACE,{"disambiguationData":[TD([[makeQuery(id+"F16.imprint","IMPRINT",EDGE,{"derivedFrom":sQuery(id+"F16.wireOp",EDGE,"E71.MirrorCS")}),-1.0]])]});
            var Q3;
            Q3=makeQuery(id+"F16.imprint","IMPRINT",FACE,{"disambiguationData":[TD([[makeQuery(id+"F16.imprint","IMPRINT",EDGE,{"derivedFrom":sQuery(id+"F16.wireOp",EDGE,"E79.MirrorCS")}),1.0]])]});
            extrude(context, id + "F17", {"entities" : qUnion([Q0, Q1, Q2, Q3]), "depth" : 1 * mm});
        }
        {
            var Q0;
            Q0=makeQuery(id+"F11.boolean.opBoolean","SPLIT",FACE,{"disambiguationData":[TD([makeQuery(id+"F3.opExtrude","SWEPT_FACE",FACE,{"disambiguationData":[OSD([sQuery(id+"F2.wireOp",EDGE,"E17.MirrorCS")])]})])],"derivedFrom":makeQuery(id+"F11.opExtrude","SWEPT_FACE",FACE,{"disambiguationData":[OSD([sQuery(id+"F10.wireOp",EDGE,"E57.MirrorCS")])]})});
            var sketch = newSketch(context, id + "F18", { "sketchPlane" : qUnion([Q0])});
            skLineSegment(sketch, "E83.bottom", {"start": v(-11.78, -49.58) * mm, "end": v(-1.78, -49.58) * mm});
            skLineSegment(sketch, "E83.top", {"start": v(-11.78, -69.58) * mm, "end": v(-1.78, -69.58) * mm});
            skLineSegment(sketch, "E83.left", {"start": v(-11.78, -49.58) * mm, "end": v(-11.78, -69.58) * mm});
            skLineSegment(sketch, "E83.right", {"start": v(-1.78, -49.58) * mm, "end": v(-1.78, -69.58) * mm});
            skPoint(sketch, "E84.endSnap0", {"position": v(-6.78, -69.58) * mm});
            skLineSegment(sketch, "E85", {"start": v(-8.28, -63.46) * mm, "end": v(-5.28, -63.46) * mm, "construction": true});
            skLineSegment(sketch, "E86", {"start": v(-6.78, -63.46) * mm, "end": v(-6.78, -65.67) * mm, "construction": true});
            skLineSegment(sketch, "E87", {"start": v(-4.78, -49.58) * mm, "end": v(-4.78, -69.58) * mm});
            skLineSegment(sketch, "E88", {"start": v(-8.78, -49.58) * mm, "end": v(-8.78, -69.58) * mm});
            skSolve(sketch);
        }
        {
            var Q0;
            {var subQ0=sQuery(id+"F18.wireOp",EDGE,"E83.left");Q0=makeQuery(id+"F18.imprint","IMPRINT",FACE,{"disambiguationData":[TD([[makeQuery(id+"F18.imprint","IMPRINT",EDGE,{"derivedFrom":subQ0}),1.0]])]});}
            var Q1;
            Q1=makeQuery(id+"F11.boolean.opBoolean","SPLIT",FACE,{"disambiguationData":[TD([makeQuery(id+"F3.opExtrude","SWEPT_FACE",FACE,{"disambiguationData":[OSD([sQuery(id+"F2.wireOp",EDGE,"E17.MirrorCS")])]})])],"derivedFrom":makeQuery(id+"F11.opExtrude","SWEPT_FACE",FACE,{"disambiguationData":[OSD([sQuery(id+"F10.wireOp",EDGE,"E56.MirrorCS")])]})});
            extrude(context, id + "F19", {"entities" : qUnion([Q0]), "endBound" : BoundingType.UP_TO_SURFACE, "oppositeDirection" : true, "endBoundEntityFace" : qUnion([Q1]), "depth" : 25 * mm});
        }
        {
            var Q0;
            {var subQ0=sQuery(id+"F18.wireOp",EDGE,"E83.left");Q0=makeQuery(id+"F18.imprint","IMPRINT",FACE,{"disambiguationData":[TD([[makeQuery(id+"F18.imprint","IMPRINT",EDGE,{"derivedFrom":subQ0}),1.0]])]});}
            var Q1;
            {var subQ0=sQuery(id+"F0.wireOp",EDGE,"E8.0");var subQ1=sQuery(id+"F2.wireOp",EDGE,"E14.MirrorCS");var subQ2=sQuery(id+"F2.wireOp",EDGE,"E16.MirrorCS");var subQ3=sQuery(id+"F10.wireOp",EDGE,"E57.MirrorCS");var subQ4=sQuery(id+"F10.wireOp",EDGE,"E58.MirrorCS");var subQ5=makeQuery(id+"F3.opExtrude","SWEPT_FACE",FACE,{"disambiguationData":[OSD([sQuery(id+"F2.wireOp",EDGE,"E17.MirrorCS")])]});var subQ18=makeQuery(id+"F11.boolean.opBoolean","SPLIT",EDGE,{"disambiguationData":[TD([subQ5])],"derivedFrom":makeQuery(id+"F11.opExtrude","SWEPT_EDGE",EDGE,{"disambiguationData":[OSD([subQ0,subQ1,subQ2,subQ3,subQ4])]})});var subQ21=sQuery(id+"F18.wireOp",EDGE,"E83.bottom");var subQ22=makeQuery(id+"F18.imprint","INTERSECT",VERTEX,{"derivedFrom":[subQ18,subQ21]});Q1=makeQuery(id+"F18.imprint","IMPRINT",FACE,{"disambiguationData":[TD([[makeQuery(id+"F18.imprint","IMPRINT",EDGE,{"disambiguationData":[TD([[subQ22,-1.0]])],"derivedFrom":subQ21}),-1.0]])]});}
            var Q2;
            {var subQ12=sQuery(id+"F18.wireOp",EDGE,"E88");Q2=makeQuery(id+"F18.imprint","IMPRINT",FACE,{"disambiguationData":[TD([[makeQuery(id+"F18.imprint","IMPRINT",EDGE,{"derivedFrom":subQ12}),1.0]])]});}
            var Q3;
            {var subQ16=sQuery(id+"F18.wireOp",EDGE,"E87");Q3=makeQuery(id+"F18.imprint","IMPRINT",FACE,{"disambiguationData":[TD([[makeQuery(id+"F18.imprint","IMPRINT",EDGE,{"derivedFrom":subQ16}),-1.0]])]});}
            var Q4;
            {var subQ0=sQuery(id+"F18.wireOp",EDGE,"E83.right");Q4=makeQuery(id+"F18.imprint","IMPRINT",FACE,{"disambiguationData":[TD([[makeQuery(id+"F18.imprint","IMPRINT",EDGE,{"derivedFrom":subQ0}),-1.0]])]});}
            extrude(context, id + "F20", {"entities" : qUnion([Q0, Q1, Q2, Q3, Q4]), "operationType" : NewBodyOperationType.ADD, "depth" : 3 * mm});
        }
        {
            var Q0;
            {var subQ0=sQuery(id+"F18.wireOp",EDGE,"E83.right");Q0=makeQuery(id+"F18.imprint","IMPRINT",FACE,{"disambiguationData":[TD([[makeQuery(id+"F18.imprint","IMPRINT",EDGE,{"derivedFrom":subQ0}),-1.0]])]});}
            extrude(context, id + "F21", {"entities" : qUnion([Q0]), "operationType" : NewBodyOperationType.ADD, "oppositeDirection" : true, "depth" : 25 * mm});
        }
        {
            var Q0;
            {var subQ0=sQuery(id+"F18.wireOp",EDGE,"E83.right");Q0=makeQuery(id+"F21.boolean.opBoolean","MERGE",FACE,{"derivedFrom":[makeQuery(id+"F20.opExtrude","SWEPT_FACE",FACE,{"disambiguationData":[OSD([subQ0])]}),makeQuery(id+"F21.opExtrude","SWEPT_FACE",FACE,{"disambiguationData":[OSD([subQ0])]})]});}
            var sketch = newSketch(context, id + "F22", { "sketchPlane" : qUnion([Q0])});
            skLineSegment(sketch, "E89.bottom", {"start": v(-69.58, 11.33) * mm, "end": v(-49.58, 11.33) * mm});
            skLineSegment(sketch, "E89.top", {"start": v(-69.58, 14.33) * mm, "end": v(-49.58, 14.33) * mm});
            skLineSegment(sketch, "E89.left", {"start": v(-69.58, 11.33) * mm, "end": v(-69.58, 14.33) * mm});
            skLineSegment(sketch, "E89.right", {"start": v(-49.58, 11.33) * mm, "end": v(-49.58, 14.33) * mm});
            skSolve(sketch);
        }
        {
            var Q0;
            Q0=makeQuery(id+"F22.imprint","IMPRINT",FACE,{"disambiguationData":[TD([[makeQuery(id+"F22.imprint","IMPRINT",EDGE,{"derivedFrom":sQuery(id+"F22.wireOp",EDGE,"E89.bottom")}),-1.0]])]});
            extrude(context, id + "F23", {"entities" : qUnion([Q0]), "operationType" : NewBodyOperationType.ADD, "depth" : 10 * mm});
        }
        {
            var Q0;
            Q0=makeQuery(id+"F23.boolean.opBoolean","MERGE",FACE,{"derivedFrom":[makeQuery(id+"F21.opExtrude","CAP_FACE",FACE,{"disambiguationData":[OSD([sQuery(id+"F18.wireOp",EDGE,"E83.bottom"),sQuery(id+"F18.wireOp",EDGE,"E83.top"),sQuery(id+"F18.wireOp",EDGE,"E83.right"),sQuery(id+"F18.wireOp",EDGE,"E87")])],"isStart":false}),makeQuery(id+"F23.opExtrude","SWEPT_FACE",FACE,{"disambiguationData":[OSD([sQuery(id+"F22.wireOp",EDGE,"E89.bottom")])]})]});
            var sketch = newSketch(context, id + "F24", { "sketchPlane" : qUnion([Q0])});
            skLineSegment(sketch, "E90.bottom", {"start": v(8.22, 69.58) * mm, "end": v(11.22, 69.58) * mm});
            skLineSegment(sketch, "E90.top", {"start": v(8.22, 49.58) * mm, "end": v(11.22, 49.58) * mm});
            skLineSegment(sketch, "E90.left", {"start": v(8.22, 69.58) * mm, "end": v(8.22, 49.58) * mm});
            skLineSegment(sketch, "E90.right", {"start": v(11.22, 69.58) * mm, "end": v(11.22, 49.58) * mm});
            skSolve(sketch);
        }
        {
            var Q0;
            Q0=makeQuery(id+"F24.imprint","IMPRINT",FACE,{"disambiguationData":[TD([[makeQuery(id+"F24.imprint","IMPRINT",EDGE,{"derivedFrom":sQuery(id+"F24.wireOp",EDGE,"E90.bottom")}),-1.0]])]});
            extrude(context, id + "F25", {"entities" : qUnion([Q0]), "operationType" : NewBodyOperationType.ADD, "oppositeDirection" : true, "depth" : 15 * mm});
        }
        {
            var Q0;
            Q0=makeQuery(id+"F25.opExtrude","CAP_EDGE",EDGE,{"disambiguationData":[OSD([sQuery(id+"F24.wireOp",EDGE,"E90.bottom")])],"isStart":false});
            var Q1;
            Q1=makeQuery(id+"F25.opExtrude","CAP_EDGE",EDGE,{"disambiguationData":[OSD([sQuery(id+"F24.wireOp",EDGE,"E90.top")])],"isStart":false});
            var Q2;
            Q2=makeQuery(id+"F25.opExtrude","CAP_EDGE",EDGE,{"disambiguationData":[OSD([sQuery(id+"F24.wireOp",EDGE,"E90.right")])],"isStart":true});
            var Q3;
            Q3=makeQuery(id+"F21.opExtrude","CAP_EDGE",EDGE,{"disambiguationData":[OSD([sQuery(id+"F18.wireOp",EDGE,"E87")])],"isStart":false});
            var Q4;
            Q4=makeQuery(id+"F20.opExtrude","CAP_EDGE",EDGE,{"disambiguationData":[OSD([sQuery(id+"F18.wireOp",EDGE,"E83.right")])],"isStart":false});
            var Q5;
            Q5=makeQuery(id+"F20.opExtrude","CAP_EDGE",EDGE,{"disambiguationData":[OSD([sQuery(id+"F18.wireOp",EDGE,"E83.left")])],"isStart":false});
            var Q6;
            Q6=makeQuery(id+"F19.opExtrude","CAP_EDGE",EDGE,{"disambiguationData":[OSD([sQuery(id+"F18.wireOp",EDGE,"E83.top")])],"isStart":false});
            var Q7;
            Q7=makeQuery(id+"F19.opExtrude","CAP_EDGE",EDGE,{"disambiguationData":[OSD([sQuery(id+"F18.wireOp",EDGE,"E83.bottom")])],"isStart":false});
            fillet(context, id + "F26", {"entities" : qUnion([Q0, Q1, Q2, Q3, Q4, Q5, Q6, Q7]), "radius" : 3 * mm, "tangentPropagation" : true, "allowEdgeOverflow" : false});
        }
    });
